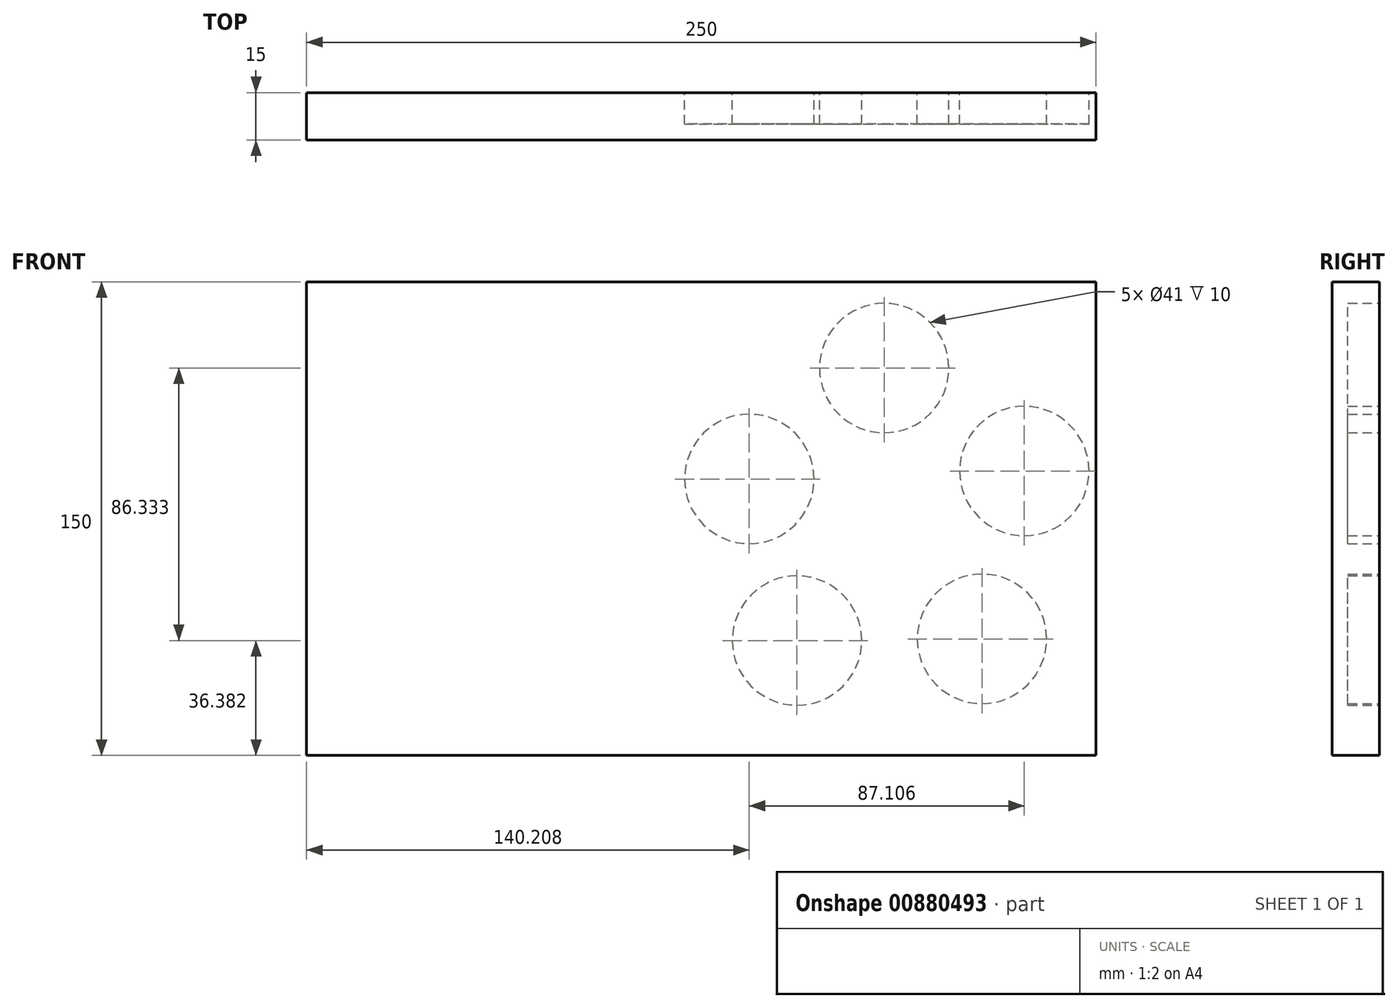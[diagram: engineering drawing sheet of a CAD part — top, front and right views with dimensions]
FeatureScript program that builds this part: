
annotation { "Feature Type Name" : "Feature", "Feature Type Description" : "" }
export const myFeature = defineFeature(function(context is Context, id is Id, definition is map)
    precondition{}
    {
        {
            var Q0;
            Q0=qCreatedBy(makeId("Front.planeOp"),FACE);
            var sketch = newSketch(context, id + "F0", { "sketchPlane" : qUnion([Q0])});
            skLineSegment(sketch, "E0.bottom", {"start": v(124.87, 79.86) * mm, "end": v(-125.13, 79.86) * mm});
            skLineSegment(sketch, "E0.top", {"start": v(124.87, -70.14) * mm, "end": v(-125.13, -70.14) * mm});
            skLineSegment(sketch, "E0.left", {"start": v(124.87, 79.86) * mm, "end": v(124.87, -70.14) * mm});
            skLineSegment(sketch, "E0.right", {"start": v(-125.13, 79.86) * mm, "end": v(-125.13, -70.14) * mm});
            skSolve(sketch);
        }
        {
            var Q0;
            Q0=makeQuery(id+"F0.imprint","IMPRINT",FACE,{"disambiguationData":[TD([[makeQuery(id+"F0.imprint","IMPRINT",EDGE,{"derivedFrom":sQuery(id+"F0.wireOp",EDGE,"E0.bottom")}),1.0]])]});
            var sketch = newSketch(context, id + "F1", { "sketchPlane" : qUnion([Q0])});
            skCircle(sketch, "E1", {"center": v(57.81, 52.57) * mm, "radius": 20.5 * mm});
            skCircle(sketch, "E2", {"center": v(102.18, 19.95) * mm, "radius": 20.5 * mm});
            skCircle(sketch, "E3", {"center": v(88.78, -33.23) * mm, "radius": 20.5 * mm});
            skCircle(sketch, "E4", {"center": v(30.2, -33.76) * mm, "radius": 20.5 * mm});
            skCircle(sketch, "E5", {"center": v(15.08, 17.43) * mm, "radius": 20.5 * mm});
            skSolve(sketch);
        }
        {
            var Q0;
            Q0=makeQuery(id+"F0.imprint","IMPRINT",FACE,{"disambiguationData":[TD([[makeQuery(id+"F0.imprint","IMPRINT",EDGE,{"derivedFrom":sQuery(id+"F0.wireOp",EDGE,"E0.bottom")}),1.0]])]});
            extrude(context, id + "F2", {"entities" : qUnion([Q0]), "depth" : 15 * mm, "offsetDistance" : 25 * mm});
        }
        {
            var Q0;
            Q0=makeQuery(id+"F1.imprint","IMPRINT",FACE,{"disambiguationData":[TD([[makeQuery(id+"F1.imprint","IMPRINT",EDGE,{"derivedFrom":sQuery(id+"F1.wireOp",EDGE,"E1")}),1.0]])]});
            var Q1;
            Q1=sQuery(id+"F1.wireOp",EDGE,"E5");
            extrude(context, id + "F3", {"entities" : qUnion([Q0]), "operationType" : NewBodyOperationType.REMOVE, "surfaceEntities" : qUnion([Q1]), "depth" : 10 * mm, "offsetDistance" : 25 * mm});
        }
        {
            var Q0;
            Q0=makeQuery(id+"F1.imprint","IMPRINT",FACE,{"disambiguationData":[TD([[makeQuery(id+"F1.imprint","IMPRINT",EDGE,{"derivedFrom":sQuery(id+"F1.wireOp",EDGE,"E2")}),1.0]])]});
            var Q1;
            Q1=sQuery(id+"F1.wireOp",EDGE,"E5");
            extrude(context, id + "F4", {"entities" : qUnion([Q0]), "operationType" : NewBodyOperationType.REMOVE, "surfaceEntities" : qUnion([Q1]), "depth" : 10 * mm, "offsetDistance" : 25 * mm});
        }
        {
            var Q0;
            Q0=makeQuery(id+"F1.imprint","IMPRINT",FACE,{"disambiguationData":[TD([[makeQuery(id+"F1.imprint","IMPRINT",EDGE,{"derivedFrom":sQuery(id+"F1.wireOp",EDGE,"E2")}),1.0]])]});
            extrude(context, id + "F5", {"entities" : qUnion([Q0]), "operationType" : NewBodyOperationType.REMOVE, "oppositeDirection" : true, "depth" : 10 * mm, "offsetDistance" : 25 * mm});
        }
        {
            var Q0;
            Q0=makeQuery(id+"F1.imprint","IMPRINT",FACE,{"disambiguationData":[TD([[makeQuery(id+"F1.imprint","IMPRINT",EDGE,{"derivedFrom":sQuery(id+"F1.wireOp",EDGE,"E3")}),1.0]])]});
            extrude(context, id + "F6", {"entities" : qUnion([Q0]), "operationType" : NewBodyOperationType.REMOVE, "depth" : 10 * mm, "offsetDistance" : 25 * mm});
        }
        {
            var Q0;
            Q0=makeQuery(id+"F1.imprint","IMPRINT",FACE,{"disambiguationData":[TD([[makeQuery(id+"F1.imprint","IMPRINT",EDGE,{"derivedFrom":sQuery(id+"F1.wireOp",EDGE,"E4")}),1.0]])]});
            extrude(context, id + "F7", {"entities" : qUnion([Q0]), "operationType" : NewBodyOperationType.REMOVE, "depth" : 10 * mm, "offsetDistance" : 25 * mm});
        }
        {
            var Q0;
            Q0=makeQuery(id+"F1.imprint","IMPRINT",FACE,{"disambiguationData":[TD([[makeQuery(id+"F1.imprint","IMPRINT",EDGE,{"derivedFrom":sQuery(id+"F1.wireOp",EDGE,"E5")}),1.0]])]});
            extrude(context, id + "F8", {"entities" : qUnion([Q0]), "operationType" : NewBodyOperationType.REMOVE, "depth" : 10 * mm, "offsetDistance" : 25 * mm});
        }
    });
